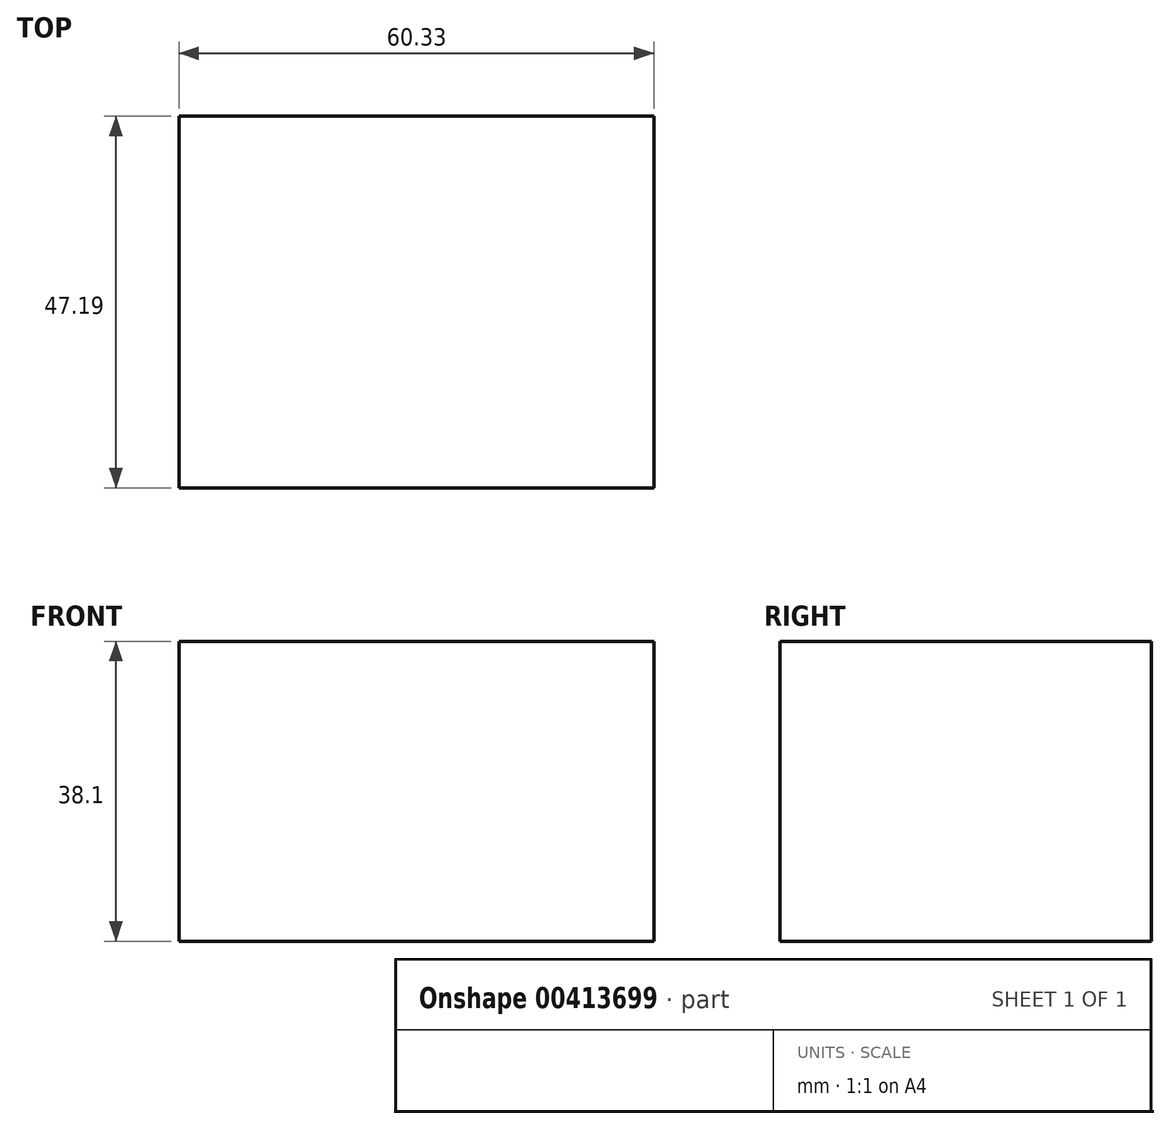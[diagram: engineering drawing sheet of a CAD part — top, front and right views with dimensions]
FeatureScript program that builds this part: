
annotation { "Feature Type Name" : "Feature", "Feature Type Description" : "" }
export const myFeature = defineFeature(function(context is Context, id is Id, definition is map)
    precondition{}
    {
        {
            var Q0;
            Q0=qCreatedBy(makeId("Top.planeOp"),FACE);
            var sketch = newSketch(context, id + "F0", { "sketchPlane" : qUnion([Q0])});
            skLineSegment(sketch, "E0.bottom", {"start": v(-139.5, 29.14) * mm, "end": v(-171.12, 29.14) * mm});
            skLineSegment(sketch, "E0.top", {"start": v(-139.5, -52.37) * mm, "end": v(-171.12, -52.37) * mm});
            skLineSegment(sketch, "E0.left", {"start": v(-139.5, 29.14) * mm, "end": v(-139.5, -52.37) * mm});
            skLineSegment(sketch, "E0.right", {"start": v(-171.12, 29.14) * mm, "end": v(-171.12, -52.37) * mm});
            skLineSegment(sketch, "E1.bottom", {"start": v(-74.6, -109.35) * mm, "end": v(-14.27, -109.35) * mm});
            skLineSegment(sketch, "E1.top", {"start": v(-74.6, -62.16) * mm, "end": v(-14.27, -62.16) * mm});
            skLineSegment(sketch, "E1.left", {"start": v(-74.6, -109.35) * mm, "end": v(-74.6, -62.16) * mm});
            skLineSegment(sketch, "E1.right", {"start": v(-14.27, -109.35) * mm, "end": v(-14.27, -62.16) * mm});
            skSolve(sketch);
        }
        {
            var Q0;
            Q0=makeQuery(id+"F0.imprint","IMPRINT",FACE,{"disambiguationData":[TD([[makeQuery(id+"F0.imprint","IMPRINT",EDGE,{"derivedFrom":sQuery(id+"F0.wireOp",EDGE,"E1.bottom")}),1.0]])]});
            extrude(context, id + "F1", {"entities" : qUnion([Q0]), "depth" : 25.4 * mm});
        }
        {
            var Q0;
            Q0=makeQuery(id+"F1.opExtrude","CAP_FACE",FACE,{"disambiguationData":[OSD([sQuery(id+"F0.wireOp",EDGE,"E1.bottom"),sQuery(id+"F0.wireOp",EDGE,"E1.top"),sQuery(id+"F0.wireOp",EDGE,"E1.left"),sQuery(id+"F0.wireOp",EDGE,"E1.right")])],"isStart":false});
            extrude(context, id + "F2", {"entities" : qUnion([Q0]), "operationType" : NewBodyOperationType.ADD, "depth" : 12.7 * mm});
        }
    });
